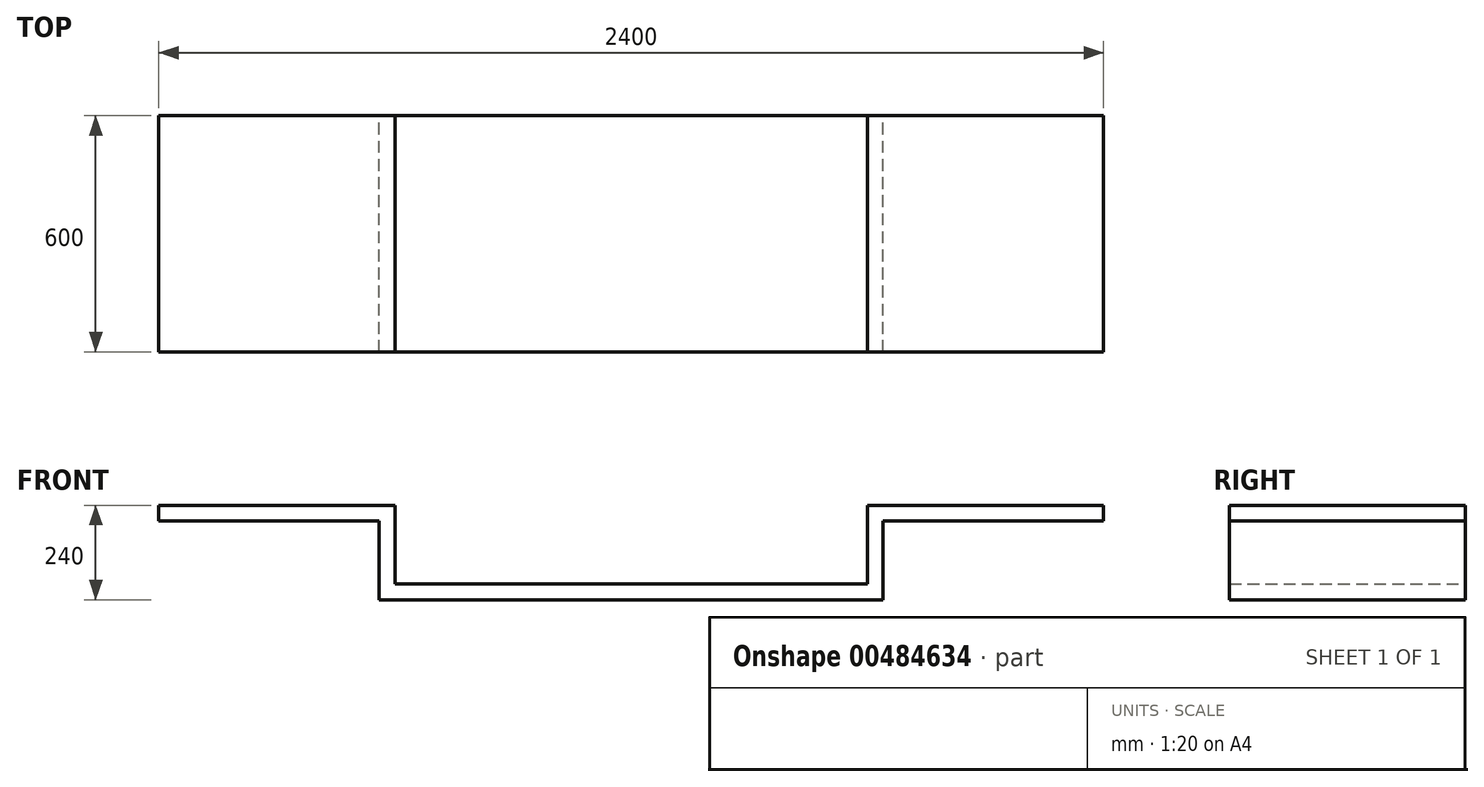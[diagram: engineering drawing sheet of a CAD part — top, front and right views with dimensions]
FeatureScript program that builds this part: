
annotation { "Feature Type Name" : "Feature", "Feature Type Description" : "" }
export const myFeature = defineFeature(function(context is Context, id is Id, definition is map)
    precondition{}
    {
        {
            var Q0;
            Q0=qCreatedBy(makeId("Front.planeOp"),FACE);
            var sketch = newSketch(context, id + "F0", { "sketchPlane" : qUnion([Q0])});
            skLineSegment(sketch, "E0", {"start": v(-1774.32, 40) * mm, "end": v(-2374.32, 40) * mm});
            skLineSegment(sketch, "E1", {"start": v(-2374.32, 40) * mm, "end": v(-2374.32, 0) * mm});
            skLineSegment(sketch, "E2", {"start": v(-2374.32, 0) * mm, "end": v(-1814.32, 0) * mm});
            skLineSegment(sketch, "E3", {"start": v(-1814.32, 0) * mm, "end": v(-1814.32, -200) * mm});
            skLineSegment(sketch, "E4", {"start": v(-1814.32, -200) * mm, "end": v(-534.32, -200) * mm});
            skLineSegment(sketch, "E5", {"start": v(-534.32, -200) * mm, "end": v(-534.32, 0) * mm});
            skLineSegment(sketch, "E6", {"start": v(-534.32, 0) * mm, "end": v(25.68, 0) * mm});
            skLineSegment(sketch, "E7", {"start": v(25.68, 0) * mm, "end": v(25.68, 40) * mm});
            skLineSegment(sketch, "E8", {"start": v(25.68, 40) * mm, "end": v(-574.32, 40) * mm});
            skLineSegment(sketch, "E9", {"start": v(-574.32, 40) * mm, "end": v(-574.32, -160) * mm});
            skLineSegment(sketch, "E10", {"start": v(-574.32, -160) * mm, "end": v(-1774.32, -160) * mm});
            skLineSegment(sketch, "E11", {"start": v(-1774.32, -160) * mm, "end": v(-1774.32, 40) * mm});
            skLineSegment(sketch, "E12", {"start": v(-1814.32, 0) * mm, "end": v(-1774.32, 40) * mm});
            skLineSegment(sketch, "E13", {"start": v(-1774.32, -160) * mm, "end": v(-1814.32, -200) * mm});
            skLineSegment(sketch, "E14", {"start": v(-574.32, -160) * mm, "end": v(-534.32, -200) * mm});
            skLineSegment(sketch, "E15", {"start": v(-534.32, 0) * mm, "end": v(-574.32, 40) * mm});
            skSolve(sketch);
        }
        {
            var Q0;
            Q0 = qSketchRegion(id + "F0", true);
            extrude(context, id + "F1", {"entities" : qUnion([Q0]), "depth" : 600 * mm});
        }
    });
